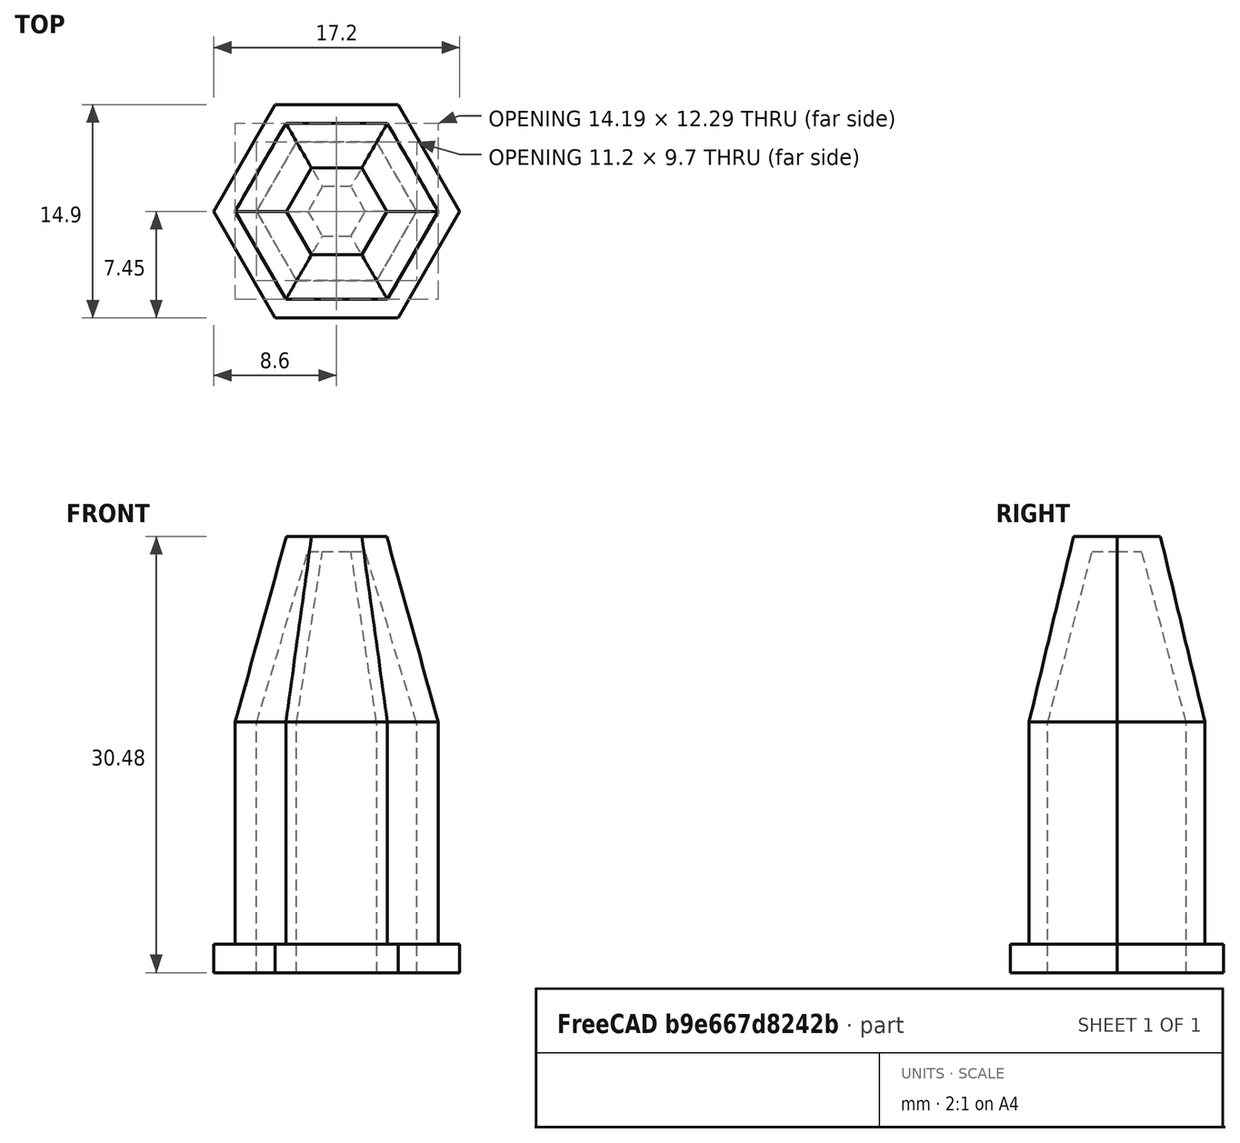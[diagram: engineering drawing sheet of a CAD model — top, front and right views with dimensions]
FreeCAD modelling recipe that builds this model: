
FCSTD DOCUMENT  (FreeCAD 0.16R6703 (Git))
Label: boli-tapa
License: All rights reserved
LicenseURL: http://en.wikipedia.org/wiki/All_rights_reserved
objects: Part::Prism×3, Part::Fuse×2, Part::Cut×2, Part::FeaturePython×2
note: 9 computed .brp shape members not serialized (recipe doc carries the construction recipe); baked Part::Feature solids carry a one-line shape summary decoded from their .brp

FEATURE [Part::Prism] prism
  Circumradius = 7.1
  Height = 17
  Placement = pos=(0,0,-8.5) rot=(0,0,1;0rad)
  Polygon = 6
FEATURE [Part::Prism] prism001
  Circumradius = 8.6
  Height = 2
  Placement = pos=(0,0,-9) rot=(0,0,1;0rad)
  Polygon = 6
FEATURE [Part::Fuse] union
  Base = -> prism
  Tool = -> prism001
FEATURE [Part::Prism] prism002
  Circumradius = 5.6
  Height = 27
  Placement = pos=(0,0,-13.5) rot=(0,0,1;0rad)
  Polygon = 6
FEATURE [Part::Cut] difference
  Base = -> union
  Placement = pos=(0,0,-8.5) rot=(0,0,1;0rad)
  Tool = -> prism002
FEATURE [Part::FeaturePython] frustum  # WARN: FeaturePython — macro-defined, semantics opaque (R4)
  FacesNumber = 6
  Height = 13
  Placement = pos=(0,0,-6.5) rot=(0,0,1;0rad)
  Radius1 = 7.1
  Radius2 = 3.5
FEATURE [Part::FeaturePython] frustum001  # WARN: FeaturePython — macro-defined, semantics opaque (R4)
  FacesNumber = 6
  Height = 12
  Placement = pos=(0,0,-6.55) rot=(0,0,1;0rad)
  Radius1 = 5.6
  Radius2 = 2
FEATURE [Part::Cut] difference001
  Base = -> frustum
  Placement = pos=(0,0,6.48) rot=(0,0,1;0rad)
  Tool = -> frustum001
FEATURE [Part::Fuse] Group
  Base = -> difference
  Tool = -> difference001
